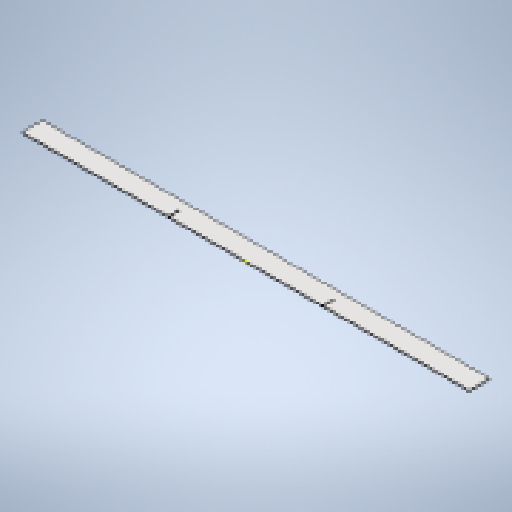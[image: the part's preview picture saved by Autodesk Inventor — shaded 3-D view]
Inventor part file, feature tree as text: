
AUTODESK INVENTOR PART (.ipt)
format: ipt  version: 2025 (Build 290162010, 162A)  size: 233,472 bytes
history: native  units: mm
features: sketch x4, extrude x2, other x2, sheet_metal_op x1, projected_geometry x1
ambient origin geometry x8: Origin, YZ Plane, XZ Plane, XY Plane, X Axis, Y Axis, Z Axis, Center Point
bodies: Body1 (feature_tree)
feature tree (10):
  sheet_metal_op  "Face1"
  extrude  "Extrusion1"  Depth=1200.0mm
  extrude  "Extrusion2"  Depth=50.0mm
  other  "Mark1"
  sketch  "Sketch1"  dims[d16=50.0mm d17=1200.0mm]
  other  "Plate2"
  sketch  "Sketch2"  dims[d18=50.0mm d19=50.0mm]
  sketch  "Sketch3"  dims[d20=3.0mm]
  projected_geometry  "Projected Loop1"
  sketch  "Sketch4"  dims[d21=190.0mm d22=3.0mm d23=26.0mm d24=0.0mm d25=0.0mm d29=190.0mm d30=3.0mm d31=26.0mm d32=2.0mm d33=8.726646mm d34=50.0mm d35=50.0mm d36=0.0mm d37=0.0mm]
